# Revit family: Accessory-Sensor_Can-KOHLER-K-23825_1
name_source: partatom
category: Specialty Equipment
units: mm (PartAtom-declared; Revit-internal decimal feet)

## family parameters
Cut with Voids When Loaded = No
Host = Face
Maintain Annotation Orientation = No
OmniClass Number = 23.31.25.00
OmniClass Title = Toilet and Bath Specialties
Part Type = Normal
Room Calculation Point = No
Round Connector Dimension = Use Diameter
Shared = No

## types (4) — shared parameters
ADA Compliant = No
Assembly Code = C1030200
Date Modified = 06/02/2022
Default Elevation = 0"
Description = 13-gallon stainless steel step trash can
Height = 26 7/16"
Length = 11"
Manufacturer = Kohler Co.
Master Format 2014 = 10 28 00
Master Format 2014 Name = Toilet, Bath, and Laundry Accessories
Material = Stainless Steel
Product Documentation Link = https://www.us.kohler.com
Product Page URL = http://www.us.kohler.com
URL = https://www.us.kohler.com
WaterSense Certified = No
Width = 16 11/16"

## per-type parameters (varying)
| type | Finish | Model | Secondary Finish | Type |
| ST-Stainless Steel | KOHLER-Metal-ST-Stainless_Steel | K-23825-ST | Kohler-Plastic-7-Black_Black | 1 |
| STW-White And Stainless Steel | KOHLER-Metal-STW-White_and_Stainless_Steel | K-23825-STW | Kohler-Plastic-0-White | 2 |
| BST-Black Stainless | KOHLER-Metal-BST-Black_Stainless | K-23825-BST | Kohler-Plastic-7-Black_Black | 3 |
| MB1-Mossy Oak Bottomlands | KOHLER-Metal-MB1-Mossy_Oak_Bottomlands | K-23825-MB1 | Kohler-Plastic-7-Black_Black | 4 |

## geometry (parser evidence)
native form markers: Sweep x4
no freeform markers — native parametric forms only
